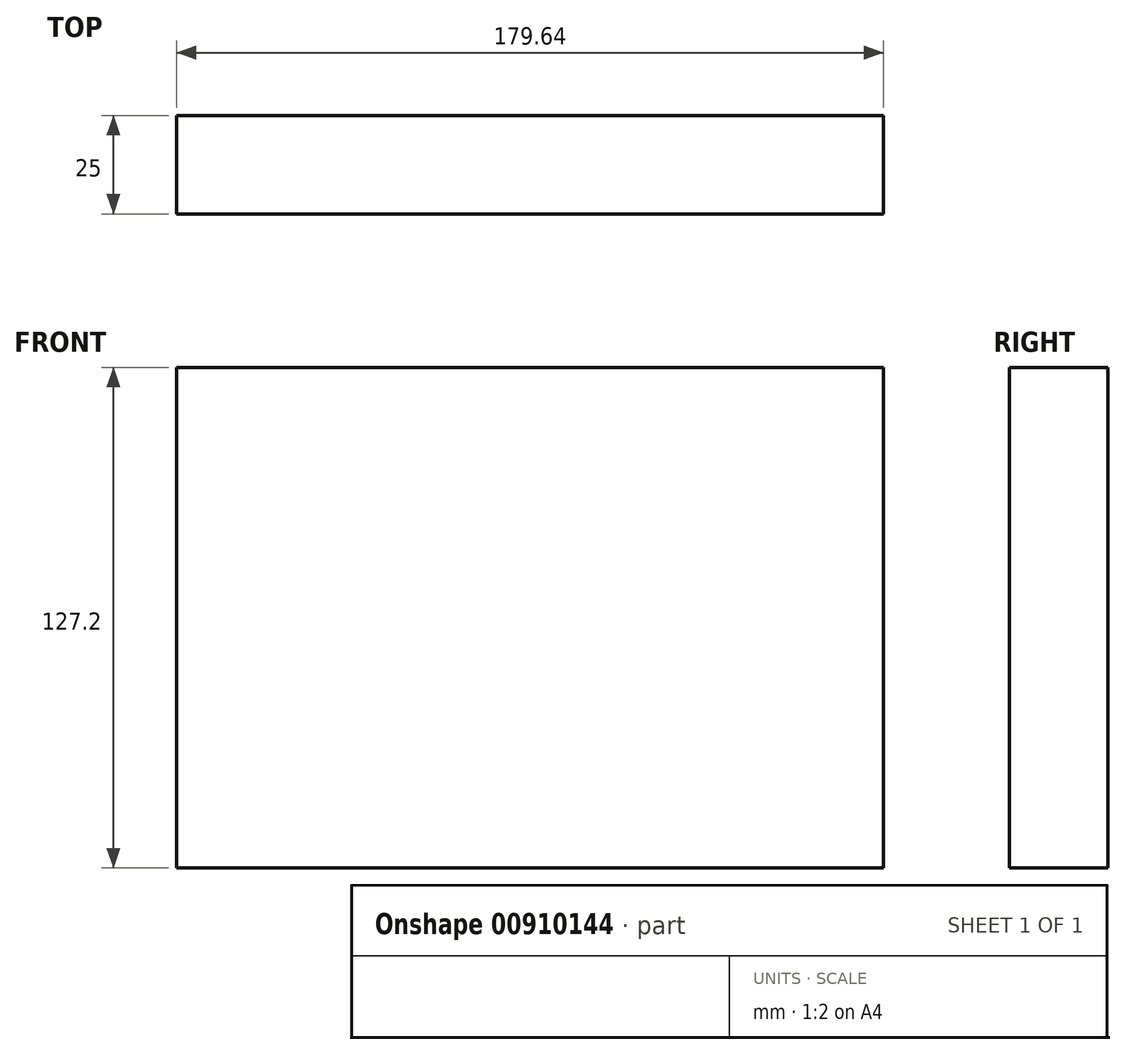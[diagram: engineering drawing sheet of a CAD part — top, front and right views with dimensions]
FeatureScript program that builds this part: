
annotation { "Feature Type Name" : "Feature", "Feature Type Description" : "" }
export const myFeature = defineFeature(function(context is Context, id is Id, definition is map)
    precondition{}
    {
        {
            var Q0;
            Q0=qCreatedBy(makeId("Front.planeOp"),FACE);
            var sketch = newSketch(context, id + "F0", { "sketchPlane" : qUnion([Q0])});
            skLineSegment(sketch, "E0.bottom", {"start": v(-27.85, 32.06) * mm, "end": v(151.8, 32.06) * mm});
            skLineSegment(sketch, "E0.top", {"start": v(-27.85, -95.14) * mm, "end": v(151.8, -95.14) * mm});
            skLineSegment(sketch, "E0.left", {"start": v(-27.85, 32.06) * mm, "end": v(-27.85, -95.14) * mm});
            skLineSegment(sketch, "E0.right", {"start": v(151.8, 32.06) * mm, "end": v(151.8, -95.14) * mm});
            skSolve(sketch);
        }
        {
            var Q0;
            Q0=makeQuery(id+"F0.imprint","IMPRINT",FACE,{"disambiguationData":[TD([[makeQuery(id+"F0.imprint","IMPRINT",EDGE,{"derivedFrom":sQuery(id+"F0.wireOp",EDGE,"E0.bottom")}),-1.0]])]});
            extrude(context, id + "F1", {"entities" : qUnion([Q0]), "depth" : 25 * mm, "offsetDistance" : 25 * mm});
        }
    });
